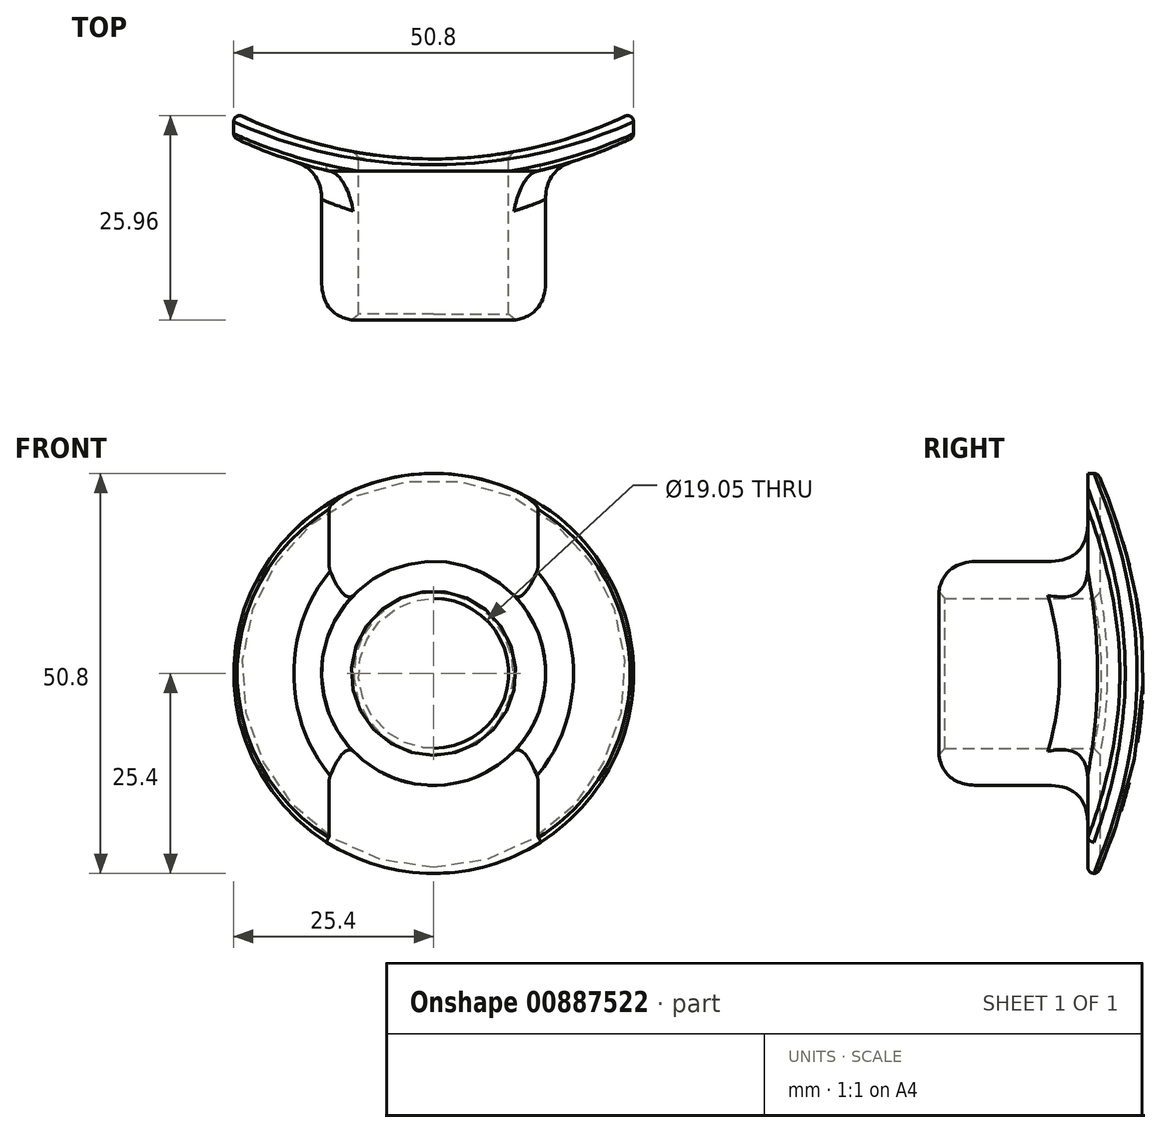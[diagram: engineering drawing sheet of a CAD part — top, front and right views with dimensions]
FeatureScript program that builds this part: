
annotation { "Feature Type Name" : "Feature", "Feature Type Description" : "" }
export const myFeature = defineFeature(function(context is Context, id is Id, definition is map)
    precondition{}
    {
        {
            var Q0;
            Q0=qCreatedBy(makeId("Front.planeOp"),FACE);
            var sketch = newSketch(context, id + "F0", { "sketchPlane" : qUnion([Q0])});
            skCircle(sketch, "E0", {"center": v(0, 0) * mm, "radius": 9.53 * mm});
            skCircle(sketch, "E1", {"center": v(0, 0) * mm, "radius": 14.22 * mm});
            skSolve(sketch);
        }
        {
            var Q0;
            Q0 = qSketchRegion(id + "F0", true);
            extrude(context, id + "F1", {"entities" : qUnion([Q0]), "depth" : 19.05 * mm, "offsetDistance" : 25.4 * mm});
        }
        {
            var Q0;
            Q0=makeQuery(id+"F1.opExtrude","CAP_FACE",FACE,{"disambiguationData":[OSD([sQuery(id+"F0.wireOp",EDGE,"E0"),sQuery(id+"F0.wireOp",EDGE,"E1")])],"isStart":true});
            var sketch = newSketch(context, id + "F2", { "sketchPlane" : qUnion([Q0])});
            skCircle(sketch, "E2", {"center": v(0, 0) * mm, "radius": 25.4 * mm});
            skCircle(sketch, "E3", {"center": v(0, 0) * mm, "radius": 9.53 * mm});
            skSolve(sketch);
        }
        {
            var Q0;
            Q0 = qSketchRegion(id + "F2", true);
            extrude(context, id + "F3", {"entities" : qUnion([Q0]), "operationType" : NewBodyOperationType.ADD, "depth" : 25.4 * mm, "offsetDistance" : 25.4 * mm});
        }
        {
            var Q0;
            Q0=qCreatedBy(makeId("Top.planeOp"),FACE);
            var sketch = newSketch(context, id + "F4", { "sketchPlane" : qUnion([Q0])});
            skCircle(sketch, "E4", {"center": v(0, 58.67) * mm, "radius": 57.15 * mm});
            skPoint(sketch, "E5.orphan", {"position": v(-60.56, 0) * mm});
            skSolve(sketch);
        }
        {
            var Q0;
            Q0 = qSketchRegion(id + "F4", true);
            extrude(context, id + "F5", {"entities" : qUnion([Q0]), "operationType" : NewBodyOperationType.REMOVE, "endBound" : BoundingType.SYMMETRIC, "depth" : 76.2 * mm, "offsetDistance" : 25.4 * mm});
        }
        {
            var Q0;
            Q0=qCreatedBy(makeId("Top.planeOp"),FACE);
            var sketch = newSketch(context, id + "F6", { "sketchPlane" : qUnion([Q0])});
            skArc(sketch, "E6", {"start": v(13.29, 0) * mm, "mid": v(0, 115.82) * mm, "end": v(-13.29, 0) * mm});
            skLineSegment(sketch, "E7.bottom", {"start": v(-25.4, 4.2) * mm, "end": v(-25.26, 4.2) * mm});
            skLineSegment(sketch, "E7.left", {"start": v(-25.4, 4.2) * mm, "end": v(-25.4, 0) * mm});
            skLineSegment(sketch, "E7.right", {"start": v(25.4, 4.2) * mm, "end": v(25.4, 0) * mm});
            skLineSegment(sketch, "E8", {"start": v(-25.4, 0) * mm, "end": v(-13.29, 0) * mm});
            skPoint(sketch, "E9.orphan", {"position": v(-27.09, 0) * mm});
            skLineSegment(sketch, "E10.trimOffspring", {"start": v(25.26, 4.2) * mm, "end": v(25.4, 4.2) * mm});
            skLineSegment(sketch, "E11.trimOffspring", {"start": v(13.29, 0) * mm, "end": v(25.4, 0) * mm});
            skSolve(sketch);
        }
        {
            var Q0;
            Q0 = qSketchRegion(id + "F6", true);
            extrude(context, id + "F7", {"entities" : qUnion([Q0]), "operationType" : NewBodyOperationType.REMOVE, "endBound" : BoundingType.SYMMETRIC, "oppositeDirection" : true, "depth" : 76.2 * mm, "offsetDistance" : 25.4 * mm});
        }
        {
            var Q0;
            {var subQ0=sQuery(id+"F0.wireOp",EDGE,"E1");Q0=makeQuery(id+"F7.boolean.opBoolean","SPLIT",EDGE,{"disambiguationData":[topologyDisambiguationEdgeConnected([makeQuery(id+"F1.opExtrude","SWEPT_FACE",FACE,{"disambiguationData":[OSD([subQ0])]}),makeQuery(id+"F7.opExtrude","SWEPT_FACE",FACE,{"disambiguationData":[OSD([sQuery(id+"F6.wireOp",EDGE,"E11.trimOffspring")])]})])],"derivedFrom":makeQuery(id+"F1.opExtrude","CAP_EDGE",EDGE,{"disambiguationData":[OSD([subQ0])],"isStart":true})});}
            var Q1;
            {var subQ0=sQuery(id+"F0.wireOp",EDGE,"E1");Q1=makeQuery(id+"F7.boolean.opBoolean","SPLIT",EDGE,{"disambiguationData":[topologyDisambiguationEdgeConnected([makeQuery(id+"F1.opExtrude","SWEPT_FACE",FACE,{"disambiguationData":[OSD([subQ0])]}),makeQuery(id+"F3.opExtrude","CAP_FACE",FACE,{"disambiguationData":[OSD([sQuery(id+"F2.wireOp",EDGE,"E2"),sQuery(id+"F2.wireOp",EDGE,"E3")])],"isStart":true})]),OD(0.0)],"derivedFrom":makeQuery(id+"F1.opExtrude","CAP_EDGE",EDGE,{"disambiguationData":[OSD([subQ0])],"isStart":true})});}
            var Q2;
            Q2=makeQuery(id+"F1.opExtrude","SWEPT_FACE",FACE,{"disambiguationData":[OSD([sQuery(id+"F0.wireOp",EDGE,"E1")])]});
            fillet(context, id + "F8", {"entities" : qUnion([Q0, Q1, Q2]), "radius" : 5.08 * mm, "tangentPropagation" : true, "rho" : 0.5, "crossSection" : FilletCrossSection.CONIC, "allowEdgeOverflow" : false});
        }
        {
            var Q0;
            {var subQ0=sQuery(id+"F6.wireOp",EDGE,"E6");Q0=makeQuery(id+"F7.boolean.opBoolean","INTERSECT",EDGE,{"disambiguationData":[OD(0.0)],"derivedFrom":[makeQuery(id+"F3.opExtrude","SWEPT_FACE",FACE,{"disambiguationData":[OSD([sQuery(id+"F2.wireOp",EDGE,"E2")])]}),makeQuery(id+"F7.opExtrude","SWEPT_FACE",FACE,{"disambiguationData":[OSD([subQ0]),TDD([makeQuery(id+"F6.imprint","IMPRINT",EDGE,{"disambiguationData":[TD([[makeQuery(id+"F6.imprint","INTERSECT",VERTEX,{"derivedFrom":[subQ0,sQuery(id+"F6.wireOp",EDGE,"E8")]}),1.0]])],"derivedFrom":subQ0})])]})]});}
            var Q1;
            Q1=makeQuery(id+"F5.boolean.opBoolean","INTERSECT",EDGE,{"derivedFrom":[makeQuery(id+"F3.opExtrude","SWEPT_FACE",FACE,{"disambiguationData":[OSD([sQuery(id+"F2.wireOp",EDGE,"E2")])]}),makeQuery(id+"F5.opExtrude","SWEPT_FACE",FACE,{"disambiguationData":[OSD([sQuery(id+"F4.wireOp",EDGE,"E4")])]})]});
            var Q2;
            {var subQ0=sQuery(id+"F6.wireOp",EDGE,"E6");Q2=makeQuery(id+"F7.boolean.opBoolean","INTERSECT",EDGE,{"disambiguationData":[OD(0.0)],"derivedFrom":[makeQuery(id+"F3.opExtrude","SWEPT_FACE",FACE,{"disambiguationData":[OSD([sQuery(id+"F2.wireOp",EDGE,"E2")])]}),makeQuery(id+"F7.opExtrude","SWEPT_FACE",FACE,{"disambiguationData":[OSD([subQ0]),TDD([makeQuery(id+"F6.imprint","IMPRINT",EDGE,{"disambiguationData":[TD([[makeQuery(id+"F6.imprint","INTERSECT",VERTEX,{"derivedFrom":[subQ0,sQuery(id+"F6.wireOp",EDGE,"E11.trimOffspring")]}),-1.0]])],"derivedFrom":subQ0})])]})]});}
            var Q3;
            {var subQ0=sQuery(id+"F6.wireOp",EDGE,"E6");Q3=makeQuery(id+"F7.boolean.opBoolean","INTERSECT",EDGE,{"disambiguationData":[OD(1.0)],"derivedFrom":[makeQuery(id+"F3.opExtrude","SWEPT_FACE",FACE,{"disambiguationData":[OSD([sQuery(id+"F2.wireOp",EDGE,"E2")])]}),makeQuery(id+"F7.opExtrude","SWEPT_FACE",FACE,{"disambiguationData":[OSD([subQ0]),TDD([makeQuery(id+"F6.imprint","IMPRINT",EDGE,{"disambiguationData":[TD([[makeQuery(id+"F6.imprint","INTERSECT",VERTEX,{"derivedFrom":[subQ0,sQuery(id+"F6.wireOp",EDGE,"E11.trimOffspring")]}),-1.0]])],"derivedFrom":subQ0})])]})]});}
            var Q4;
            Q4=makeQuery(id+"F7.boolean.opBoolean","INTERSECT",EDGE,{"derivedFrom":[makeQuery(id+"F3.opExtrude","SWEPT_FACE",FACE,{"disambiguationData":[OSD([sQuery(id+"F2.wireOp",EDGE,"E2")])]}),makeQuery(id+"F7.opExtrude","SWEPT_FACE",FACE,{"disambiguationData":[OSD([sQuery(id+"F6.wireOp",EDGE,"E10.trimOffspring")])]})]});
            var Q5;
            Q5=makeQuery(id+"F7.boolean.opBoolean","SPLIT",EDGE,{"disambiguationData":[OD(1.0)],"derivedFrom":makeQuery(id+"F3.opExtrude","CAP_EDGE",EDGE,{"disambiguationData":[OSD([sQuery(id+"F2.wireOp",EDGE,"E2")])],"isStart":true})});
            fillet(context, id + "F9", {"entities" : qUnion([Q0, Q1, Q2, Q3, Q4, Q5]), "radius" : 0.76 * mm, "tangentPropagation" : true, "allowEdgeOverflow" : false});
        }
        {
            var Q0;
            Q0=makeQuery(id+"F5.boolean.opBoolean","INTERSECT",EDGE,{"derivedFrom":[makeQuery(id+"F3.boolean.opBoolean","MERGE",FACE,{"derivedFrom":[makeQuery(id+"F1.opExtrude","SWEPT_FACE",FACE,{"disambiguationData":[OSD([sQuery(id+"F0.wireOp",EDGE,"E0")])]}),makeQuery(id+"F3.opExtrude","SWEPT_FACE",FACE,{"disambiguationData":[OSD([sQuery(id+"F2.wireOp",EDGE,"E3")])]})]}),makeQuery(id+"F5.opExtrude","SWEPT_FACE",FACE,{"disambiguationData":[OSD([sQuery(id+"F4.wireOp",EDGE,"E4")])]})]});
            var Q1;
            Q1=makeQuery(id+"F8.opFillet","BLEND_EDGE",EDGE,{"blendedFrom":[makeQuery(id+"F1.opExtrude","CAP_EDGE",EDGE,{"disambiguationData":[OSD([sQuery(id+"F0.wireOp",EDGE,"E1")])],"isStart":false}),makeQuery(id+"F3.boolean.opBoolean","MERGE",FACE,{"derivedFrom":[makeQuery(id+"F1.opExtrude","SWEPT_FACE",FACE,{"disambiguationData":[OSD([sQuery(id+"F0.wireOp",EDGE,"E0")])]}),makeQuery(id+"F3.opExtrude","SWEPT_FACE",FACE,{"disambiguationData":[OSD([sQuery(id+"F2.wireOp",EDGE,"E3")])]})]})],"blendedInto":[makeQuery(id+"F3.boolean.opBoolean","MERGE",FACE,{"derivedFrom":[makeQuery(id+"F1.opExtrude","SWEPT_FACE",FACE,{"disambiguationData":[OSD([sQuery(id+"F0.wireOp",EDGE,"E0")])]}),makeQuery(id+"F3.opExtrude","SWEPT_FACE",FACE,{"disambiguationData":[OSD([sQuery(id+"F2.wireOp",EDGE,"E3")])]})]})]});
            chamfer(context, id + "F10", {"entities" : qUnion([Q0, Q1]), "width" : 0.76 * mm, "tangentPropagation" : true});
        }
    });
